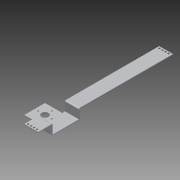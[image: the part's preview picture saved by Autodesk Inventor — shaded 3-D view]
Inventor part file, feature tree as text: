
AUTODESK INVENTOR PART (.ipt)
format: ipt  version: 2013 (Build 170138000, 138)  size: 290,304 bytes
history: native  units: in
note: dims shown in document units (in); Inventor stores cm internally (conversion verified against a paired STEP export)
features: sheet_metal_op x10, reference x8, other x6, sketch x5, projected_geometry x1
ambient origin geometry x8: Origin, YZ Plane, XZ Plane, XY Plane, X Axis, Y Axis, Z Axis, Center Point
bodies: Solid1 (feature_tree)
feature tree (30):
  sheet_metal_op  "Face1"
  sheet_metal_op  "Flange1"
  sheet_metal_op  "Flange2"
  sheet_metal_op  "Flange3"
  sketch  "Sketch1"  dims[d0=1.0in]
  other  "Plate1"
  sketch  "Sketch2"  dims[d1=1.0in]
  other  "Plate2"
  sheet_metal_op  "Bend1"
  sheet_metal_op  "Corner1"
  sketch  "Sketch3"  dims[d2=1.0in]
  other  "Plate3"
  sheet_metal_op  "Bend2"
  sheet_metal_op  "Corner2"
  sketch  "Sketch4"  dims[d3=0.5in]
  other  "Plate4"
  sheet_metal_op  "Bend3"
  sheet_metal_op  "Corner3"
  sketch  "Sketch5"  dims[d4=2.0in d5=2.0in d6=0.5in d7=2.0in d8=0.125in d9=0.125in d10=0.0625in d11=0.25in d12=0.125in d13=1.5in d14=90.0deg d15=0.05in d16=0.5in d17=0.125in d18=0.125in d19=0.125in d20=0.0625in d21=0.25in d22=0.125in d23=2.125in d24=90.0deg d25=0.05in d26=0.5in d27=0.125in d28=0.125in d29=0.125in d30=0.0625in d31=0.25in d32=0.125in d33=13.625in d34=90.0deg d35=0.05in d36=0.5in d37=0.125in d38=0.125in d39=0.125in d40=0.0in]
  projected_geometry  "Projected Loop1"
  reference  "Reference1"
  reference  "Reference2"
  reference  "Reference3"
  reference  "Reference4"
  reference  "Reference5"
  reference  "Reference6"
  reference  "Reference7"
  reference  "Reference8"
  other  "Cut1"
  other  "Definition1"
